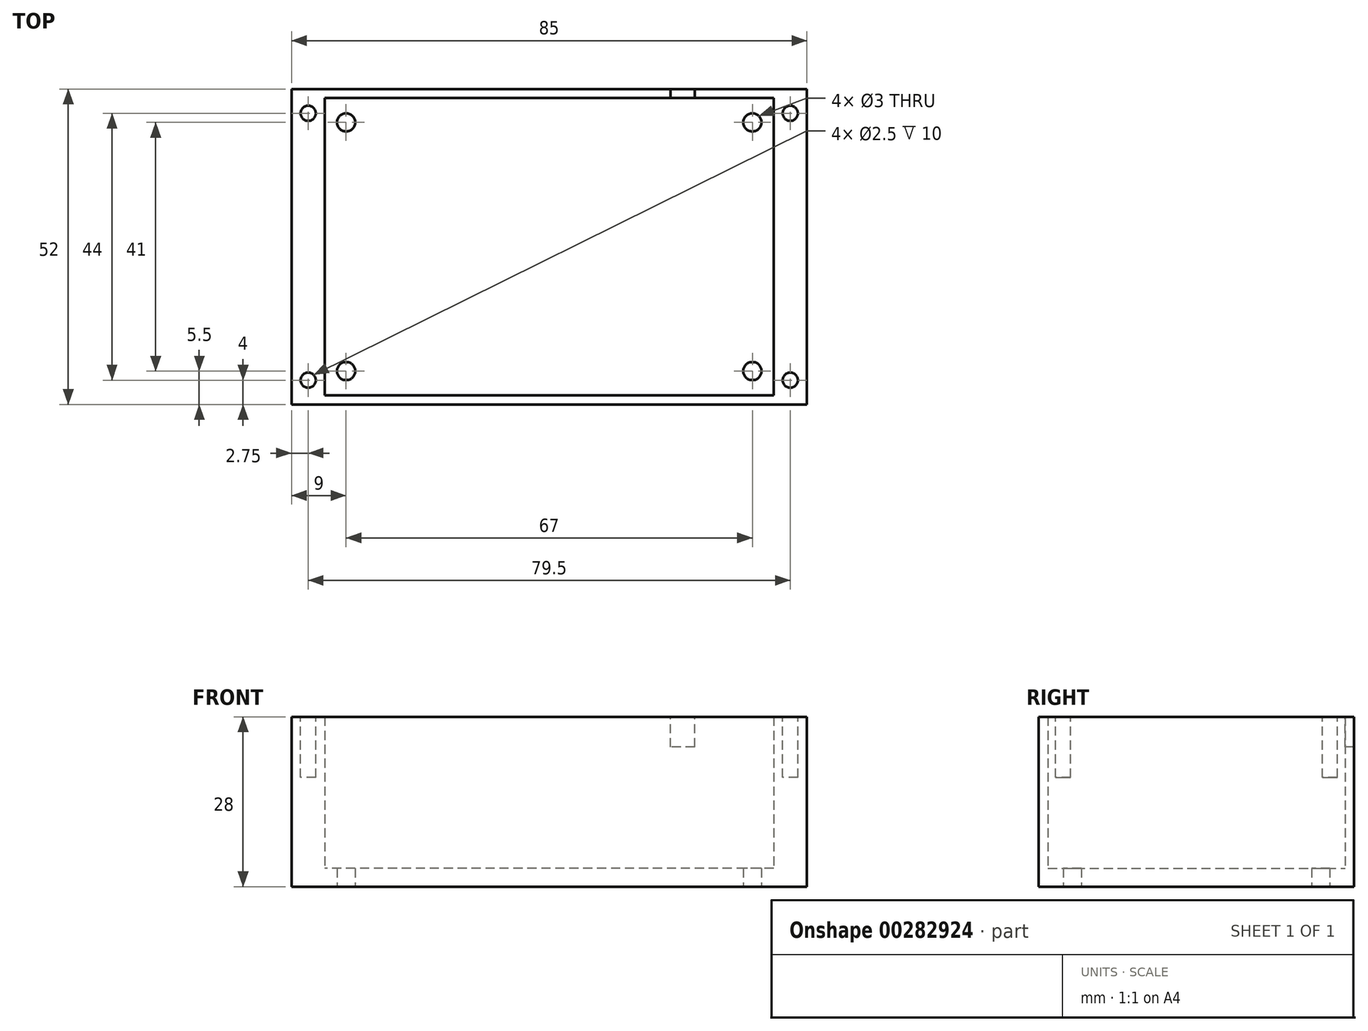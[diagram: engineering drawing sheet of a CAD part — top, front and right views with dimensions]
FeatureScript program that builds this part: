
annotation { "Feature Type Name" : "Feature", "Feature Type Description" : "" }
export const myFeature = defineFeature(function(context is Context, id is Id, definition is map)
    precondition{}
    {
        {
            var Q0;
            Q0=qCreatedBy(makeId("Top.planeOp"),FACE);
            var sketch = newSketch(context, id + "F0", { "sketchPlane" : qUnion([Q0])});
            skLineSegment(sketch, "E0.bottom", {"start": v(42.5, -26) * mm, "end": v(-42.5, -26) * mm});
            skLineSegment(sketch, "E0.top", {"start": v(42.5, 26) * mm, "end": v(-42.5, 26) * mm});
            skLineSegment(sketch, "E0.left", {"start": v(42.5, -26) * mm, "end": v(42.5, 26) * mm});
            skLineSegment(sketch, "E0.right", {"start": v(-42.5, -26) * mm, "end": v(-42.5, 26) * mm});
            skPoint(sketch, "E0.middle", {"position": v(0, 0) * mm});
            skLineSegment(sketch, "E1", {"start": v(0, 0) * mm, "end": v(33.5, 0) * mm, "construction": true});
            skLineSegment(sketch, "E2", {"start": v(0, 0) * mm, "end": v(-33.5, 0) * mm, "construction": true});
            skLineSegment(sketch, "E3", {"start": v(-33.5, 0) * mm, "end": v(-33.5, 20.5) * mm, "construction": true});
            skLineSegment(sketch, "E4", {"start": v(-33.5, 0) * mm, "end": v(-33.5, -20.5) * mm, "construction": true});
            skLineSegment(sketch, "E5", {"start": v(33.5, 0) * mm, "end": v(33.5, 20.5) * mm, "construction": true});
            skLineSegment(sketch, "E6", {"start": v(33.5, 0) * mm, "end": v(33.5, -20.5) * mm, "construction": true});
            skCircle(sketch, "E7", {"center": v(-33.5, 20.5) * mm, "radius": 1.5 * mm});
            skCircle(sketch, "E8", {"center": v(33.5, 20.5) * mm, "radius": 1.5 * mm});
            skCircle(sketch, "E9", {"center": v(-33.5, -20.5) * mm, "radius": 1.5 * mm});
            skCircle(sketch, "E10", {"center": v(33.5, -20.5) * mm, "radius": 1.5 * mm});
            skSolve(sketch);
        }
        {
            var Q0;
            Q0 = qSketchRegion(id + "F0", true);
            extrude(context, id + "F1", {"entities" : qUnion([Q0]), "depth" : 3 * mm});
        }
        {
            var Q0;
            Q0=makeQuery(id+"F1.opExtrude","CAP_FACE",FACE,{"disambiguationData":[OSD([sQuery(id+"F0.wireOp",EDGE,"E0.bottom"),sQuery(id+"F0.wireOp",EDGE,"E0.top"),sQuery(id+"F0.wireOp",EDGE,"E0.left"),sQuery(id+"F0.wireOp",EDGE,"E0.right"),sQuery(id+"F0.wireOp",EDGE,"E7"),sQuery(id+"F0.wireOp",EDGE,"E8"),sQuery(id+"F0.wireOp",EDGE,"E9"),sQuery(id+"F0.wireOp",EDGE,"E10")])],"isStart":false});
            var sketch = newSketch(context, id + "F2", { "sketchPlane" : qUnion([Q0])});
            skLineSegment(sketch, "E11.bottom", {"start": v(37, -24.5) * mm, "end": v(-37, -24.5) * mm});
            skLineSegment(sketch, "E11.top", {"start": v(37, 24.5) * mm, "end": v(-37, 24.5) * mm});
            skLineSegment(sketch, "E11.left", {"start": v(37, -24.5) * mm, "end": v(37, 24.5) * mm});
            skLineSegment(sketch, "E11.right", {"start": v(-37, -24.5) * mm, "end": v(-37, 24.5) * mm});
            skPoint(sketch, "E11.middle", {"position": v(0, 0) * mm});
            skLineSegment(sketch, "E12.bottom", {"start": v(-42.5, 26) * mm, "end": v(42.5, 26) * mm});
            skLineSegment(sketch, "E12.top", {"start": v(-42.5, -26) * mm, "end": v(42.5, -26) * mm});
            skLineSegment(sketch, "E12.left", {"start": v(-42.5, 26) * mm, "end": v(-42.5, -26) * mm});
            skLineSegment(sketch, "E12.right", {"start": v(42.5, 26) * mm, "end": v(42.5, -26) * mm});
            skSolve(sketch);
        }
        {
            var Q0;
            Q0 = qSketchRegion(id + "F2", true);
            extrude(context, id + "F3", {"entities" : qUnion([Q0]), "operationType" : NewBodyOperationType.ADD, "depth" : 25 * mm});
        }
        {
            var Q0;
            Q0=makeQuery(id+"F3.opExtrude","CAP_FACE",FACE,{"disambiguationData":[OSD([sQuery(id+"F2.wireOp",EDGE,"E11.bottom"),sQuery(id+"F2.wireOp",EDGE,"E11.top"),sQuery(id+"F2.wireOp",EDGE,"E11.left"),sQuery(id+"F2.wireOp",EDGE,"E11.right"),sQuery(id+"F2.wireOp",EDGE,"E12.bottom"),sQuery(id+"F2.wireOp",EDGE,"E12.top"),sQuery(id+"F2.wireOp",EDGE,"E12.left"),sQuery(id+"F2.wireOp",EDGE,"E12.right")])],"isStart":false});
            var sketch = newSketch(context, id + "F4", { "sketchPlane" : qUnion([Q0])});
            skLineSegment(sketch, "E13", {"start": v(-42.5, 26) * mm, "end": v(-39.75, 26) * mm, "construction": true});
            skLineSegment(sketch, "E14", {"start": v(-39.75, 26) * mm, "end": v(-39.75, 22) * mm, "construction": true});
            skCircle(sketch, "E15", {"center": v(-39.75, 22) * mm, "radius": 1.25 * mm});
            skCircle(sketch, "E16.MirrorC", {"center": v(-39.75, -22) * mm, "radius": 1.25 * mm});
            skCircle(sketch, "E17.MirrorC", {"center": v(39.75, 22) * mm, "radius": 1.25 * mm});
            skCircle(sketch, "E18.MirrorC", {"center": v(39.75, -22) * mm, "radius": 1.25 * mm});
            skSolve(sketch);
        }
        {
            var Q0;
            Q0 = qSketchRegion(id + "F4", true);
            extrude(context, id + "F5", {"entities" : qUnion([Q0]), "operationType" : NewBodyOperationType.REMOVE, "oppositeDirection" : true, "depth" : 10 * mm});
        }
        {
            var Q0;
            Q0=makeQuery(id+"F3.opExtrude","CAP_FACE",FACE,{"disambiguationData":[OSD([sQuery(id+"F2.wireOp",EDGE,"E11.bottom"),sQuery(id+"F2.wireOp",EDGE,"E11.top"),sQuery(id+"F2.wireOp",EDGE,"E11.left"),sQuery(id+"F2.wireOp",EDGE,"E11.right"),sQuery(id+"F2.wireOp",EDGE,"E12.bottom"),sQuery(id+"F2.wireOp",EDGE,"E12.top"),sQuery(id+"F2.wireOp",EDGE,"E12.left"),sQuery(id+"F2.wireOp",EDGE,"E12.right")])],"isStart":false});
            var sketch = newSketch(context, id + "F6", { "sketchPlane" : qUnion([Q0])});
            skLineSegment(sketch, "E19", {"start": v(20, 26) * mm, "end": v(20, 24.5) * mm});
            skLineSegment(sketch, "E20", {"start": v(20, 24.5) * mm, "end": v(24, 24.5) * mm});
            skLineSegment(sketch, "E21", {"start": v(24, 24.5) * mm, "end": v(24, 26) * mm});
            skLineSegment(sketch, "E22", {"start": v(24, 26) * mm, "end": v(20, 26) * mm});
            skSolve(sketch);
        }
        {
            var Q0;
            Q0 = qSketchRegion(id + "F6", true);
            extrude(context, id + "F7", {"entities" : qUnion([Q0]), "operationType" : NewBodyOperationType.REMOVE, "oppositeDirection" : true, "depth" : 5 * mm});
        }
    });
